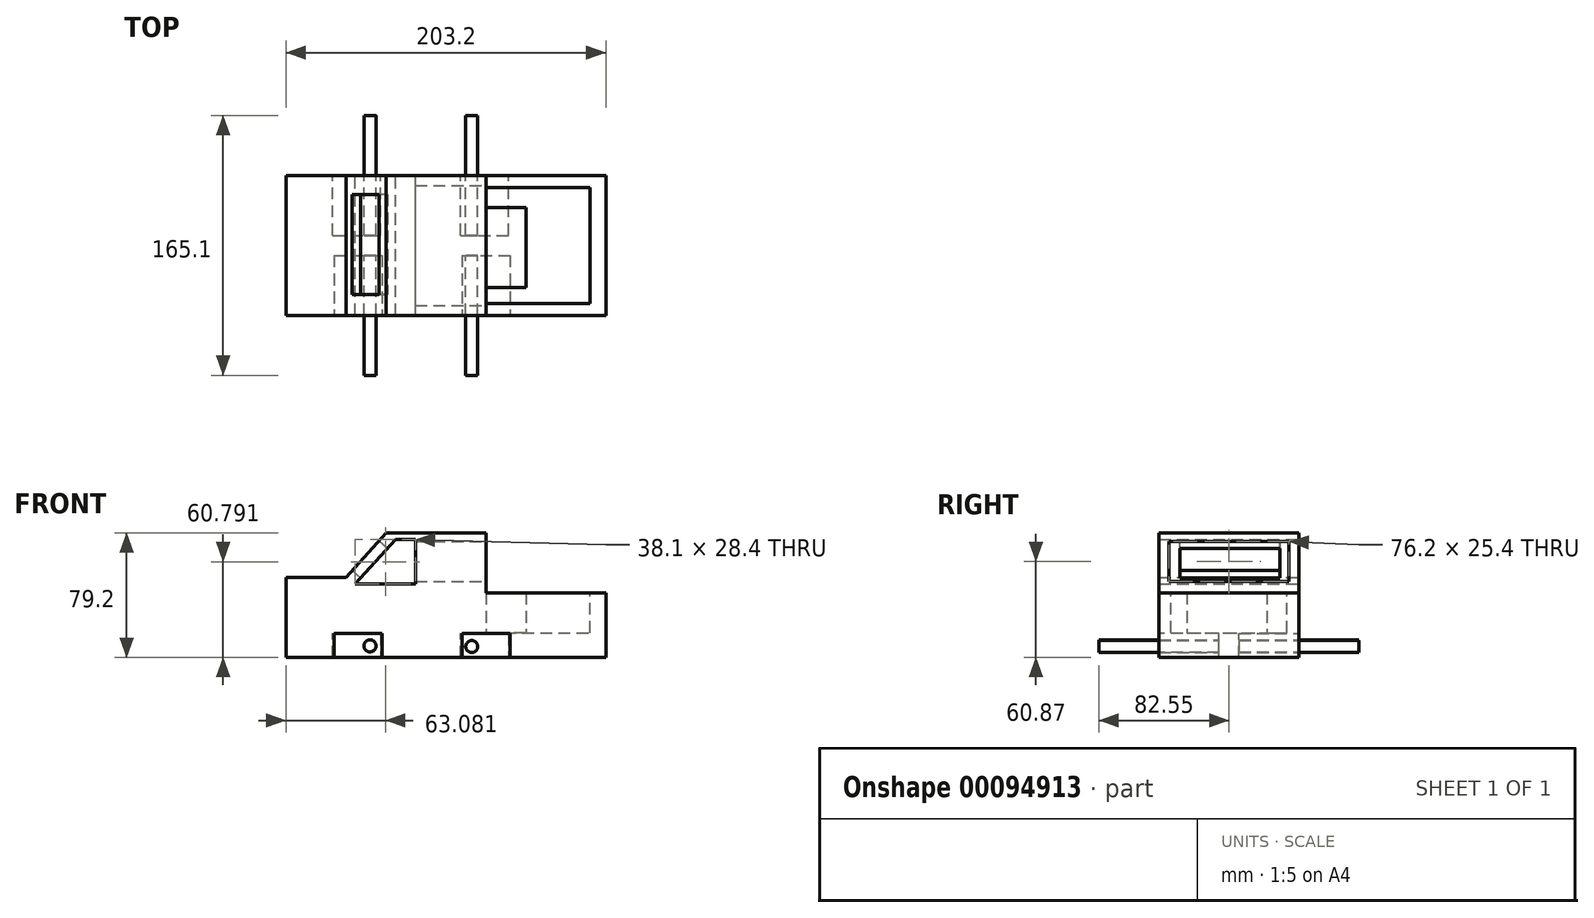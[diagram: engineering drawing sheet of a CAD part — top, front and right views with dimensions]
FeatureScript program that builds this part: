
annotation { "Feature Type Name" : "Feature", "Feature Type Description" : "" }
export const myFeature = defineFeature(function(context is Context, id is Id, definition is map)
    precondition{}
    {
        {
            var Q0;
            Q0=qCreatedBy(makeId("Front.planeOp"),FACE);
            var sketch = newSketch(context, id + "F0", { "sketchPlane" : qUnion([Q0])});
            skLineSegment(sketch, "E0", {"start": v(0, 0) * mm, "end": v(203.2, 0) * mm});
            skLineSegment(sketch, "E1", {"start": v(0, 0) * mm, "end": v(0, 50.8) * mm});
            skLineSegment(sketch, "E2", {"start": v(0, 50.8) * mm, "end": v(38.1, 50.8) * mm});
            skLineSegment(sketch, "E3", {"start": v(38.1, 50.8) * mm, "end": v(63.5, 79.2) * mm});
            skLineSegment(sketch, "E4", {"start": v(63.5, 79.2) * mm, "end": v(127, 79.2) * mm});
            skLineSegment(sketch, "E5", {"start": v(127, 79.2) * mm, "end": v(127, 41.1) * mm});
            skLineSegment(sketch, "E6", {"start": v(127, 41.1) * mm, "end": v(203.2, 41.1) * mm});
            skLineSegment(sketch, "E7", {"start": v(203.2, 41.1) * mm, "end": v(203.2, 0) * mm});
            skLineSegment(sketch, "E8", {"start": v(29.54, 0) * mm, "end": v(29.54, 15.24) * mm});
            skLineSegment(sketch, "E9", {"start": v(29.54, 15.24) * mm, "end": v(60.02, 15.24) * mm});
            skLineSegment(sketch, "E10", {"start": v(60.02, 15.24) * mm, "end": v(60.02, 0) * mm});
            skLineSegment(sketch, "E11", {"start": v(60.02, 0) * mm, "end": v(29.54, 0) * mm});
            skLineSegment(sketch, "E12", {"start": v(121.12, 0) * mm, "end": v(121.12, 15.24) * mm});
            skLineSegment(sketch, "E13", {"start": v(121.12, 15.24) * mm, "end": v(151.6, 15.24) * mm});
            skLineSegment(sketch, "E14", {"start": v(151.6, 15.24) * mm, "end": v(151.6, 0) * mm});
            skSolve(sketch);
        }
        {
            var Q0;
            Q0 = qSketchRegion(id + "F0", true);
            extrude(context, id + "F1", {"entities" : qUnion([Q0]), "depth" : 88.9 * mm});
        }
        {
            var Q0;
            Q0=makeQuery(id+"F1.opExtrude","CAP_FACE",FACE,{"disambiguationData":[OSD([sQuery(id+"F0.wireOp",EDGE,"E0"),sQuery(id+"F0.wireOp",EDGE,"E1"),sQuery(id+"F0.wireOp",EDGE,"E2"),sQuery(id+"F0.wireOp",EDGE,"E3"),sQuery(id+"F0.wireOp",EDGE,"E4"),sQuery(id+"F0.wireOp",EDGE,"E5"),sQuery(id+"F0.wireOp",EDGE,"E6"),sQuery(id+"F0.wireOp",EDGE,"E7"),sQuery(id+"F0.wireOp",EDGE,"E11")])],"isStart":false});
            var sketch = newSketch(context, id + "F2", { "sketchPlane" : qUnion([Q0])});
            skLineSegment(sketch, "E15", {"start": v(30.65, 0) * mm, "end": v(30.65, 15.24) * mm});
            skLineSegment(sketch, "E16", {"start": v(30.65, 15.24) * mm, "end": v(61.13, 15.24) * mm});
            skLineSegment(sketch, "E17", {"start": v(61.13, 15.24) * mm, "end": v(61.13, 0) * mm});
            skLineSegment(sketch, "E18", {"start": v(61.13, 0) * mm, "end": v(30.65, 0) * mm});
            skLineSegment(sketch, "E19", {"start": v(111.93, 0) * mm, "end": v(111.93, 15.24) * mm});
            skLineSegment(sketch, "E20", {"start": v(111.93, 15.24) * mm, "end": v(142.41, 15.24) * mm});
            skLineSegment(sketch, "E21", {"start": v(142.41, 15.24) * mm, "end": v(142.41, 0) * mm});
            skLineSegment(sketch, "E22", {"start": v(142.41, 0) * mm, "end": v(111.93, 0) * mm});
            skSolve(sketch);
        }
        {
            var Q0;
            Q0=makeQuery(id+"F2.imprint","IMPRINT",FACE,{"disambiguationData":[TD([[makeQuery(id+"F2.imprint","IMPRINT",EDGE,{"derivedFrom":sQuery(id+"F2.wireOp",EDGE,"E15")}),-1.0]])]});
            var Q1;
            Q1=makeQuery(id+"F2.imprint","IMPRINT",FACE,{"disambiguationData":[TD([[makeQuery(id+"F2.imprint","IMPRINT",EDGE,{"derivedFrom":sQuery(id+"F2.wireOp",EDGE,"E19")}),-1.0]])]});
            extrude(context, id + "F3", {"entities" : qUnion([Q0, Q1]), "operationType" : NewBodyOperationType.REMOVE, "oppositeDirection" : true, "depth" : 38.1 * mm});
        }
        {
            var Q0;
            Q0=makeQuery(id+"F1.opExtrude","CAP_FACE",FACE,{"disambiguationData":[OSD([sQuery(id+"F0.wireOp",EDGE,"E0"),sQuery(id+"F0.wireOp",EDGE,"E1"),sQuery(id+"F0.wireOp",EDGE,"E2"),sQuery(id+"F0.wireOp",EDGE,"E3"),sQuery(id+"F0.wireOp",EDGE,"E4"),sQuery(id+"F0.wireOp",EDGE,"E5"),sQuery(id+"F0.wireOp",EDGE,"E6"),sQuery(id+"F0.wireOp",EDGE,"E7"),sQuery(id+"F0.wireOp",EDGE,"E11")])],"isStart":true});
            var sketch = newSketch(context, id + "F4", { "sketchPlane" : qUnion([Q0])});
            skLineSegment(sketch, "E23", {"start": v(-29.54, 0) * mm, "end": v(-29.54, 15.24) * mm});
            skLineSegment(sketch, "E24", {"start": v(-29.54, 15.24) * mm, "end": v(-60.02, 15.24) * mm});
            skLineSegment(sketch, "E25", {"start": v(-60.02, 15.24) * mm, "end": v(-60.02, 0) * mm});
            skLineSegment(sketch, "E26", {"start": v(-60.02, 0) * mm, "end": v(-29.54, 0) * mm});
            skLineSegment(sketch, "E27", {"start": v(-110.82, 0) * mm, "end": v(-110.82, 15.24) * mm});
            skLineSegment(sketch, "E28", {"start": v(-110.82, 15.24) * mm, "end": v(-141.3, 15.24) * mm});
            skLineSegment(sketch, "E29", {"start": v(-141.3, 15.24) * mm, "end": v(-141.3, 0) * mm});
            skLineSegment(sketch, "E30", {"start": v(-141.3, 0) * mm, "end": v(-110.82, 0) * mm});
            skSolve(sketch);
        }
        {
            var Q0;
            Q0=makeQuery(id+"F4.imprint","IMPRINT",FACE,{"disambiguationData":[TD([[makeQuery(id+"F4.imprint","IMPRINT",EDGE,{"derivedFrom":sQuery(id+"F4.wireOp",EDGE,"E27")}),1.0]])]});
            var Q1;
            Q1=makeQuery(id+"F4.imprint","IMPRINT",FACE,{"disambiguationData":[TD([[makeQuery(id+"F4.imprint","IMPRINT",EDGE,{"derivedFrom":sQuery(id+"F4.wireOp",EDGE,"E23")}),1.0]])]});
            extrude(context, id + "F5", {"entities" : qUnion([Q0, Q1]), "operationType" : NewBodyOperationType.REMOVE, "oppositeDirection" : true, "depth" : 38.1 * mm});
        }
        {
            var Q0;
            Q0=qCreatedBy(makeId("Front.planeOp"),FACE);
            var sketch = newSketch(context, id + "F6", { "sketchPlane" : qUnion([Q0])});
            skCircle(sketch, "E31", {"center": v(53.35, 7.34) * mm, "radius": 3.81 * mm});
            skCircle(sketch, "E32", {"center": v(117.93, 6.96) * mm, "radius": 3.81 * mm});
            skSolve(sketch);
        }
        {
            var Q0;
            Q0=makeQuery(id+"F6.imprint","IMPRINT",FACE,{"disambiguationData":[TD([[makeQuery(id+"F6.imprint","IMPRINT",EDGE,{"derivedFrom":sQuery(id+"F6.wireOp",EDGE,"E31")}),1.0]])]});
            var Q1;
            Q1=makeQuery(id+"F6.imprint","IMPRINT",FACE,{"disambiguationData":[TD([[makeQuery(id+"F6.imprint","IMPRINT",EDGE,{"derivedFrom":sQuery(id+"F6.wireOp",EDGE,"E32")}),1.0]])]});
            extrude(context, id + "F7", {"entities" : qUnion([Q0, Q1]), "operationType" : NewBodyOperationType.ADD, "depth" : 127 * mm, "hasSecondDirection" : true, "secondDirectionOppositeDirection" : true, "secondDirectionDepth" : 38.1 * mm});
        }
        {
            var Q0;
            Q0=qCreatedBy(makeId("Front.planeOp"),FACE);
            var sketch = newSketch(context, id + "F8", { "sketchPlane" : qUnion([Q0])});
            skLineSegment(sketch, "E33", {"start": v(44.03, 46.6) * mm, "end": v(69.43, 74.99) * mm});
            skLineSegment(sketch, "E34", {"start": v(69.43, 74.99) * mm, "end": v(82.13, 74.99) * mm});
            skLineSegment(sketch, "E35", {"start": v(44.03, 46.6) * mm, "end": v(82.13, 46.6) * mm});
            skLineSegment(sketch, "E36", {"start": v(82.13, 74.99) * mm, "end": v(82.13, 46.6) * mm});
            skSolve(sketch);
        }
        {
            var Q0;
            Q0 = qSketchRegion(id + "F8", true);
            extrude(context, id + "F9", {"entities" : qUnion([Q0]), "operationType" : NewBodyOperationType.REMOVE, "depth" : 88.9 * mm});
        }
        {
            var Q0;
            Q0=makeQuery(id+"F1.opExtrude","SWEPT_FACE",FACE,{"disambiguationData":[OSD([sQuery(id+"F0.wireOp",EDGE,"E6")])]});
            var sketch = newSketch(context, id + "F10", { "sketchPlane" : qUnion([Q0])});
            skLineSegment(sketch, "E37", {"start": v(127, -81.28) * mm, "end": v(193.04, -81.28) * mm});
            skLineSegment(sketch, "E38", {"start": v(193.04, -81.28) * mm, "end": v(193.04, -7.62) * mm});
            skLineSegment(sketch, "E39", {"start": v(193.04, -7.62) * mm, "end": v(127, -7.62) * mm});
            skLineSegment(sketch, "E40", {"start": v(127, -7.62) * mm, "end": v(127, -81.28) * mm});
            skSolve(sketch);
        }
        {
            var Q0;
            Q0=makeQuery(id+"F10.imprint","IMPRINT",FACE,{"disambiguationData":[TD([[makeQuery(id+"F10.imprint","IMPRINT",EDGE,{"derivedFrom":sQuery(id+"F10.wireOp",EDGE,"E37")}),1.0]])]});
            extrude(context, id + "F11", {"entities" : qUnion([Q0]), "operationType" : NewBodyOperationType.REMOVE, "oppositeDirection" : true, "depth" : 25.4 * mm});
        }
        {
            var Q0;
            Q0=makeQuery(id+"F1.opExtrude","SWEPT_FACE",FACE,{"disambiguationData":[OSD([sQuery(id+"F0.wireOp",EDGE,"E3")])]});
            var sketch = newSketch(context, id + "F12", { "sketchPlane" : qUnion([Q0])});
            skLineSegment(sketch, "E41", {"start": v(12.1, 94.59) * mm, "end": v(12.1, 69.19) * mm});
            skLineSegment(sketch, "E42", {"start": v(12.1, 69.19) * mm, "end": v(75.6, 69.19) * mm});
            skLineSegment(sketch, "E43", {"start": v(75.6, 69.19) * mm, "end": v(75.6, 94.59) * mm});
            skLineSegment(sketch, "E44", {"start": v(12.1, 94.59) * mm, "end": v(75.6, 94.59) * mm});
            skSolve(sketch);
        }
        {
            var Q0;
            Q0 = qSketchRegion(id + "F12", true);
            extrude(context, id + "F13", {"entities" : qUnion([Q0]), "operationType" : NewBodyOperationType.REMOVE, "oppositeDirection" : true, "depth" : 12.7 * mm});
        }
        {
            var Q0;
            Q0=makeQuery(id+"F1.opExtrude","SWEPT_FACE",FACE,{"disambiguationData":[OSD([sQuery(id+"F0.wireOp",EDGE,"E1")])]});
            var sketch = newSketch(context, id + "F14", { "sketchPlane" : qUnion([Q0])});
            skLineSegment(sketch, "E45", {"start": v(6.08, 41.8) * mm, "end": v(31.48, 41.8) * mm});
            skLineSegment(sketch, "E46", {"start": v(31.48, 41.8) * mm, "end": v(31.48, 35.46) * mm});
            skLineSegment(sketch, "E47", {"start": v(31.48, 35.46) * mm, "end": v(6.08, 35.46) * mm});
            skLineSegment(sketch, "E48", {"start": v(6.08, 35.46) * mm, "end": v(6.08, 41.8) * mm});
            skLineSegment(sketch, "E49", {"start": v(56.88, 41.8) * mm, "end": v(83.68, 41.8) * mm});
            skLineSegment(sketch, "E50", {"start": v(83.68, 41.8) * mm, "end": v(83.68, 35.46) * mm});
            skLineSegment(sketch, "E51", {"start": v(83.68, 35.46) * mm, "end": v(56.88, 35.46) * mm});
            skLineSegment(sketch, "E52", {"start": v(56.88, 35.46) * mm, "end": v(56.88, 41.8) * mm});
            skSolve(sketch);
        }
        {
            var Q0;
            Q0=makeQuery(id+"F11.boolean.opBoolean","MERGE",FACE,{"derivedFrom":[makeQuery(id+"F1.opExtrude","SWEPT_FACE",FACE,{"disambiguationData":[OSD([sQuery(id+"F0.wireOp",EDGE,"E5")])]}),makeQuery(id+"F11.opExtrude","SWEPT_FACE",FACE,{"disambiguationData":[OSD([sQuery(id+"F10.wireOp",EDGE,"E40")])]})]});
            var sketch = newSketch(context, id + "F15", { "sketchPlane" : qUnion([Q0])});
            skLineSegment(sketch, "E53", {"start": v(-82.55, 48.17) * mm, "end": v(-82.55, 73.57) * mm});
            skLineSegment(sketch, "E54", {"start": v(-82.55, 48.17) * mm, "end": v(-6.35, 48.17) * mm});
            skLineSegment(sketch, "E55", {"start": v(-6.35, 48.17) * mm, "end": v(-6.35, 73.57) * mm});
            skLineSegment(sketch, "E56", {"start": v(-6.35, 73.57) * mm, "end": v(-82.55, 73.57) * mm});
            skSolve(sketch);
        }
        {
            var Q0;
            Q0=makeQuery(id+"F15.imprint","IMPRINT",FACE,{"disambiguationData":[TD([[makeQuery(id+"F15.imprint","IMPRINT",EDGE,{"derivedFrom":sQuery(id+"F15.wireOp",EDGE,"E53")}),-1.0]])]});
            extrude(context, id + "F16", {"entities" : qUnion([Q0]), "operationType" : NewBodyOperationType.REMOVE, "oppositeDirection" : true, "depth" : 50.8 * mm});
        }
        {
            var Q0;
            Q0=makeQuery(id+"F14.imprint","IMPRINT",FACE,{"disambiguationData":[TD([[makeQuery(id+"F14.imprint","IMPRINT",EDGE,{"derivedFrom":sQuery(id+"F14.wireOp",EDGE,"E45")}),1.0]])]});
            var sketch = newSketch(context, id + "F17", { "sketchPlane" : qUnion([Q0])});
            skLineSegment(sketch, "E57", {"start": v(56.95, 31.6) * mm, "end": v(56.95, 26.28) * mm});
            skLineSegment(sketch, "E58", {"start": v(56.95, 31.6) * mm, "end": v(37.37, 31.6) * mm});
            skLineSegment(sketch, "E59", {"start": v(37.37, 31.6) * mm, "end": v(37.37, 26.03) * mm});
            skLineSegment(sketch, "E60", {"start": v(37.37, 26.03) * mm, "end": v(24.8, 26.03) * mm});
            skLineSegment(sketch, "E61", {"start": v(24.8, 26.03) * mm, "end": v(27.46, 18.78) * mm});
            skLineSegment(sketch, "E62", {"start": v(27.46, 18.78) * mm, "end": v(37.6, 18.78) * mm});
            skLineSegment(sketch, "E63", {"start": v(37.6, 18.78) * mm, "end": v(37.6, 13.95) * mm});
            skLineSegment(sketch, "E64", {"start": v(37.6, 13.95) * mm, "end": v(56.7, 13.95) * mm});
            skLineSegment(sketch, "E65", {"start": v(56.7, 13.95) * mm, "end": v(56.7, 18.78) * mm});
            skLineSegment(sketch, "E66", {"start": v(56.7, 18.78) * mm, "end": v(68.07, 18.78) * mm});
            skLineSegment(sketch, "E67", {"start": v(56.95, 26.28) * mm, "end": v(63.71, 26.28) * mm});
            skLineSegment(sketch, "E68", {"start": v(68.07, 18.78) * mm, "end": v(63.71, 26.28) * mm});
            skSolve(sketch);
        }
        {
            var Q0;
            Q0 = qSketchRegion(id + "F17", true);
            extrude(context, id + "F18", {"entities" : qUnion([Q0]), "operationType" : NewBodyOperationType.ADD, "oppositeDirection" : true, "depth" : 7.62 * mm});
        }
        {
            var Q0;
            Q0=makeQuery(id+"F14.imprint","IMPRINT",FACE,{"disambiguationData":[TD([[makeQuery(id+"F14.imprint","IMPRINT",EDGE,{"derivedFrom":sQuery(id+"F14.wireOp",EDGE,"E45")}),1.0]])]});
            var sketch = newSketch(context, id + "F19", { "sketchPlane" : qUnion([Q0])});
            skCircle(sketch, "E69", {"center": v(40.63, 25.05) * mm, "radius": 18.29 * mm});
            skLineSegment(sketch, "E70", {"start": v(40.63, 25.05) * mm, "end": v(40.63, 43.34) * mm});
            skLineSegment(sketch, "E71", {"start": v(40.63, 25.05) * mm, "end": v(40.63, 6.77) * mm});
            skLineSegment(sketch, "E72", {"start": v(33.74, 42) * mm, "end": v(33.74, 8.11) * mm});
            skLineSegment(sketch, "E73", {"start": v(47.9, 41.82) * mm, "end": v(47.9, 8.28) * mm});
            skLineSegment(sketch, "E74", {"start": v(26.98, 37.22) * mm, "end": v(26.98, 12.88) * mm});
            skLineSegment(sketch, "E75", {"start": v(55.36, 35.88) * mm, "end": v(55.36, 14.22) * mm});
            skSolve(sketch);
        }
        {
            var Q0;
            Q0 = qSketchRegion(id + "FRlql23m4ECYKr3_1", true);
            var Q1;
            Q1=makeQuery(id+"F19.imprint","IMPRINT",FACE,{"disambiguationData":[TD([[makeQuery(id+"F19.imprint","IMPRINT",EDGE,{"derivedFrom":makeQuery(id+"F14.imprint","IMPRINT",EDGE,{"derivedFrom":sQuery(id+"F14.wireOp",EDGE,"E49")})}),-1.0]])]});
            var Q2;
            Q2=makeQuery(id+"F14.imprint","IMPRINT",FACE,{"disambiguationData":[TD([[makeQuery(id+"F14.imprint","IMPRINT",EDGE,{"derivedFrom":sQuery(id+"F14.wireOp",EDGE,"E45")}),-1.0]])]});
            extrude(context, id + "F20", {"entities" : qUnion([Q0, Q1, Q2]), "operationType" : NewBodyOperationType.ADD, "depth" : 12.7 * mm});
        }
        {
            var Q0;
            Q0=makeQuery(id+"F20.opExtrude","CAP_FACE",FACE,{"disambiguationData":[OSD([sQuery(id+"F14.wireOp",EDGE,"E45"),sQuery(id+"F14.wireOp",EDGE,"E46"),sQuery(id+"F14.wireOp",EDGE,"E47"),sQuery(id+"F14.wireOp",EDGE,"E48")])],"isStart":false});
            var Q1;
            Q1=makeQuery(id+"F20.opExtrude","CAP_FACE",FACE,{"disambiguationData":[OSD([sQuery(id+"F14.wireOp",EDGE,"E49"),sQuery(id+"F14.wireOp",EDGE,"E50"),sQuery(id+"F14.wireOp",EDGE,"E51"),sQuery(id+"F14.wireOp",EDGE,"E52")])],"isStart":false});
            extrude(context, id + "F21", {"entities" : qUnion([Q0, Q1]), "operationType" : NewBodyOperationType.REMOVE, "oppositeDirection" : true, "depth" : 12.7 * mm});
        }
        {
            var Q0;
            Q0=makeQuery(id+"F11.boolean.opBoolean","MERGE",FACE,{"derivedFrom":[makeQuery(id+"F1.opExtrude","SWEPT_FACE",FACE,{"disambiguationData":[OSD([sQuery(id+"F0.wireOp",EDGE,"E5")])]}),makeQuery(id+"F11.opExtrude","SWEPT_FACE",FACE,{"disambiguationData":[OSD([sQuery(id+"F10.wireOp",EDGE,"E40")])]})]});
            var sketch = newSketch(context, id + "F22", { "sketchPlane" : qUnion([Q0])});
            skLineSegment(sketch, "E76", {"start": v(-71.12, 41.1) * mm, "end": v(-20.32, 41.1) * mm});
            skLineSegment(sketch, "E77", {"start": v(-20.32, 41.1) * mm, "end": v(-20.32, 15.7) * mm});
            skLineSegment(sketch, "E78", {"start": v(-71.12, 41.1) * mm, "end": v(-71.12, 15.7) * mm});
            skLineSegment(sketch, "E79", {"start": v(-71.12, 15.7) * mm, "end": v(-20.32, 15.7) * mm});
            skSolve(sketch);
        }
        {
            var Q0;
            Q0 = qSketchRegion(id + "F22", true);
            extrude(context, id + "F23", {"entities" : qUnion([Q0]), "operationType" : NewBodyOperationType.ADD, "depth" : 38.1 * mm});
        }
        {
            var Q0;
            Q0=makeQuery(id+"F23.opExtrude","CAP_FACE",FACE,{"disambiguationData":[OSD([sQuery(id+"F22.wireOp",EDGE,"E76"),sQuery(id+"F22.wireOp",EDGE,"E77"),sQuery(id+"F22.wireOp",EDGE,"E78"),sQuery(id+"F22.wireOp",EDGE,"E79")])],"isStart":false});
            extrude(context, id + "F24", {"entities" : qUnion([Q0]), "operationType" : NewBodyOperationType.REMOVE, "oppositeDirection" : true, "depth" : 12.7 * mm});
        }
    });
